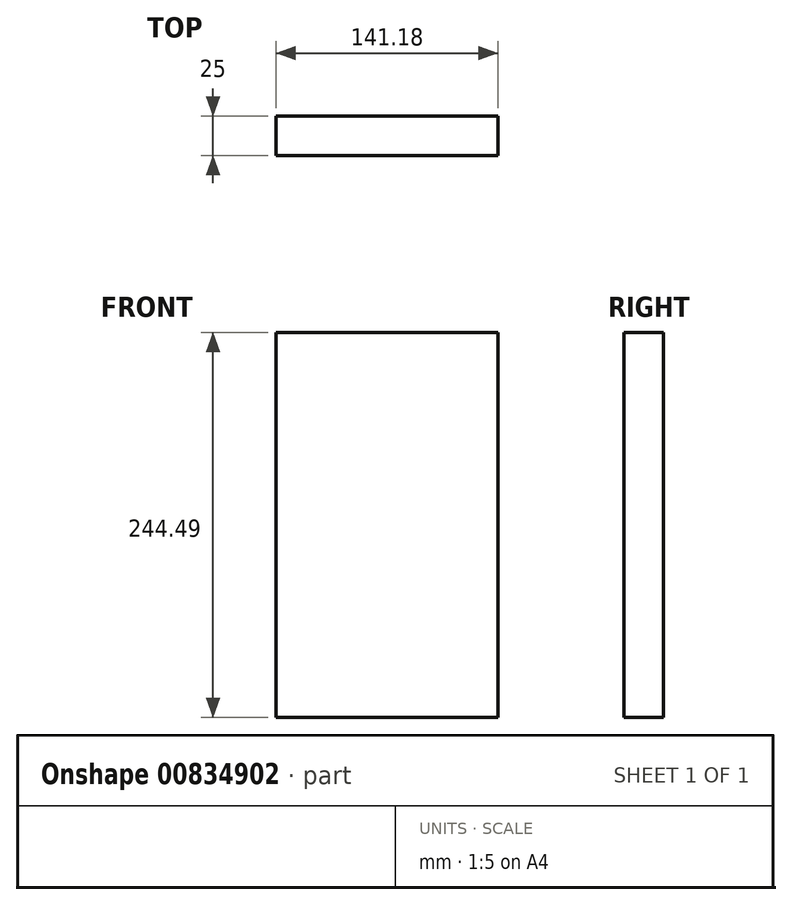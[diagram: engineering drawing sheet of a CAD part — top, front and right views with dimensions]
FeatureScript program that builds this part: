
annotation { "Feature Type Name" : "Feature", "Feature Type Description" : "" }
export const myFeature = defineFeature(function(context is Context, id is Id, definition is map)
    precondition{}
    {
        {
            var Q0;
            Q0=qCreatedBy(makeId("Front.planeOp"),FACE);
            var sketch = newSketch(context, id + "F0", { "sketchPlane" : qUnion([Q0])});
            skLineSegment(sketch, "E0", {"start": v(-65.65, 167.33) * mm, "end": v(-65.65, -77.16) * mm});
            skLineSegment(sketch, "E1", {"start": v(-65.65, -77.16) * mm, "end": v(75.53, -77.16) * mm});
            skLineSegment(sketch, "E2", {"start": v(75.53, -77.16) * mm, "end": v(75.53, 167.33) * mm});
            skLineSegment(sketch, "E3", {"start": v(75.53, 167.33) * mm, "end": v(-65.65, 167.33) * mm});
            skSolve(sketch);
        }
        {
            var Q0;
            Q0 = qSketchRegion(id + "F0", true);
            extrude(context, id + "F1", {"entities" : qUnion([Q0]), "depth" : 25 * mm, "offsetDistance" : 25 * mm});
        }
    });
